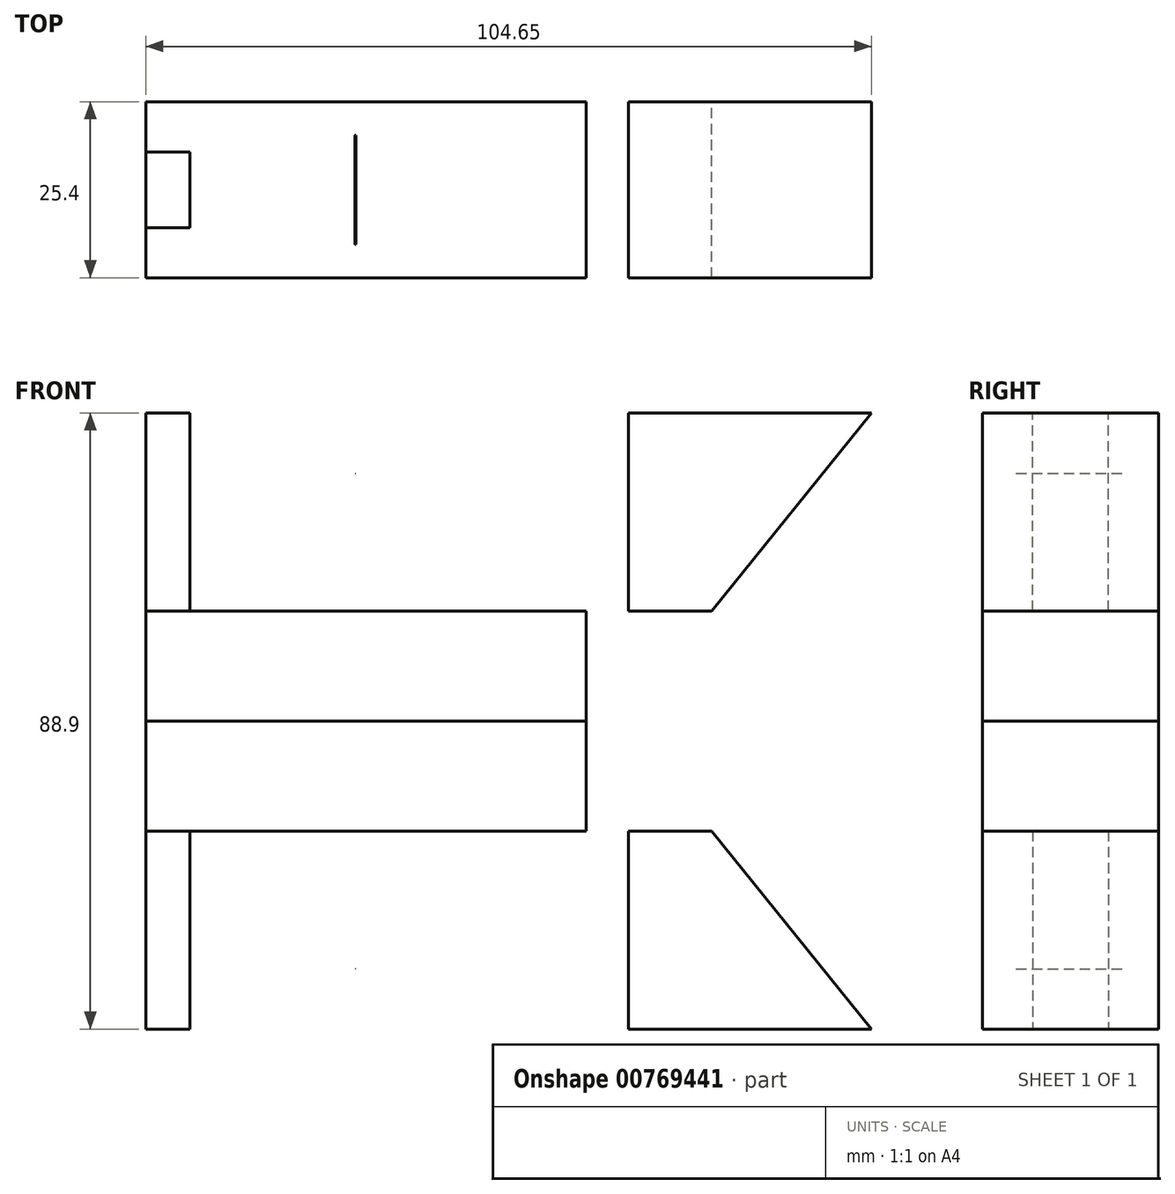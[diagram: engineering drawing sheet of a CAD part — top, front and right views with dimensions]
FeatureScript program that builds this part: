
annotation { "Feature Type Name" : "Feature", "Feature Type Description" : "" }
export const myFeature = defineFeature(function(context is Context, id is Id, definition is map)
    precondition{}
    {
        {
            var Q0;
            Q0=qCreatedBy(makeId("Front.planeOp"),FACE);
            var sketch = newSketch(context, id + "F0", { "sketchPlane" : qUnion([Q0])});
            skLineSegment(sketch, "E0.bottom", {"start": v(-31.75, 7.94) * mm, "end": v(31.75, 7.94) * mm});
            skLineSegment(sketch, "E0.top", {"start": v(-31.75, -7.94) * mm, "end": v(31.75, -7.94) * mm});
            skLineSegment(sketch, "E0.left", {"start": v(-31.75, 7.94) * mm, "end": v(-31.75, -7.94) * mm});
            skLineSegment(sketch, "E0.right", {"start": v(31.75, 7.94) * mm, "end": v(31.75, -7.94) * mm});
            skPoint(sketch, "E0.middle", {"position": v(0, 0) * mm});
            skLineSegment(sketch, "E1.bottom", {"start": v(-31.75, 7.94) * mm, "end": v(72.9, 7.94) * mm});
            skLineSegment(sketch, "E1.top", {"start": v(-31.75, 36.51) * mm, "end": v(72.9, 36.51) * mm});
            skLineSegment(sketch, "E1.left", {"start": v(-31.75, 7.94) * mm, "end": v(-31.75, 36.51) * mm});
            skLineSegment(sketch, "E1.right", {"start": v(72.9, 7.94) * mm, "end": v(72.9, 36.51) * mm});
            skLineSegment(sketch, "E2", {"start": v(-25.4, 36.51) * mm, "end": v(-25.4, 7.94) * mm});
            skLineSegment(sketch, "E3", {"start": v(72.9, 36.51) * mm, "end": v(49.83, 7.94) * mm});
            skLineSegment(sketch, "E4", {"start": v(-31.75, 22.23) * mm, "end": v(-7.11, 22.23) * mm});
            skLineSegment(sketch, "E5", {"start": v(-7.11, 22.23) * mm, "end": v(27.94, 22.23) * mm});
            skCircle(sketch, "E6", {"center": v(-1.52, 22.23) * mm, "radius": 5.59 * mm});
            skCircle(sketch, "E7", {"center": v(22.05, 22.23) * mm, "radius": 5.59 * mm});
            skLineSegment(sketch, "E8", {"start": v(-1.56, 27.81) * mm, "end": v(22.05, 27.81) * mm});
            skLineSegment(sketch, "E9", {"start": v(-1.44, 16.64) * mm, "end": v(22.05, 16.64) * mm});
            skLineSegment(sketch, "E10", {"start": v(37.85, 36.51) * mm, "end": v(37.85, 7.94) * mm});
            skLineSegment(sketch, "E11", {"start": v(37.85, 18.99) * mm, "end": v(58.75, 18.99) * mm});
            skSolve(sketch);
        }
        {
            var Q0;
            Q0=makeQuery(id+"F0.imprint","IMPRINT",FACE,{"disambiguationData":[TD([[makeQuery(id+"F0.imprint","IMPRINT",EDGE,{"derivedFrom":sQuery(id+"F0.wireOp",EDGE,"E0.top")}),1.0]])]});
            var Q1;
            {var subQ5=sQuery(id+"F0.wireOp",EDGE,"E11");Q1=makeQuery(id+"F0.imprint","IMPRINT",FACE,{"disambiguationData":[TD([[makeQuery(id+"F0.imprint","IMPRINT",EDGE,{"derivedFrom":subQ5}),1.0]])]});}
            var Q2;
            {var subQ5=sQuery(id+"F0.wireOp",EDGE,"E11");Q2=makeQuery(id+"F0.imprint","IMPRINT",FACE,{"disambiguationData":[TD([[makeQuery(id+"F0.imprint","IMPRINT",EDGE,{"derivedFrom":subQ5}),-1.0]])]});}
            extrude(context, id + "F1", {"entities" : qUnion([Q0, Q1, Q2]), "depth" : 25.4 * mm, "offsetDistance" : 25.4 * mm, "symmetric" : true});
        }
        {
            var Q0;
            {var subQ7=sQuery(id+"F0.wireOp",EDGE,"E8");Q0=makeQuery(id+"F0.imprint","IMPRINT",FACE,{"disambiguationData":[TD([[makeQuery(id+"F0.imprint","IMPRINT",EDGE,{"derivedFrom":subQ7}),1.0]])]});}
            extrude(context, id + "F2", {"entities" : qUnion([Q0]), "depth" : 15.75 * mm, "offsetDistance" : 25.4 * mm, "symmetric" : true});
        }
        {
            var Q0;
            {var subQ0=sQuery(id+"F0.wireOp",EDGE,"E1.left");var subQ1=sQuery(id+"F0.wireOp",EDGE,"E1.top");var subQ2=makeQuery(id+"F0.imprint","INTERSECT",VERTEX,{"derivedFrom":[subQ1,subQ0]});Q0=makeQuery(id+"F0.imprint","IMPRINT",FACE,{"disambiguationData":[TD([[makeQuery(id+"F0.imprint","IMPRINT",EDGE,{"disambiguationData":[TD([[subQ2,-1.0]])],"derivedFrom":subQ1}),-1.0]])]});}
            var Q1;
            {var subQ1=sQuery(id+"F0.wireOp",EDGE,"E1.bottom");var subQ3=sQuery(id+"F0.wireOp",EDGE,"E2");var subQ4=makeQuery(id+"F0.imprint","INTERSECT",VERTEX,{"derivedFrom":[subQ1,subQ3]});Q1=makeQuery(id+"F0.imprint","IMPRINT",FACE,{"disambiguationData":[TD([[makeQuery(id+"F0.imprint","IMPRINT",EDGE,{"disambiguationData":[TD([[subQ4,1.0]])],"derivedFrom":subQ3}),-1.0]])]});}
            extrude(context, id + "F3", {"entities" : qUnion([Q0, Q1]), "depth" : 10.92 * mm, "offsetDistance" : 25.4 * mm, "symmetric" : true});
        }
        {
            var Q0;
            Q0=makeQuery(id+"F3.opExtrude","SWEPT_BODY",BODY,{"disambiguationData":[OSD([sQuery(id+"F0.wireOp",EDGE,"E1.bottom"),sQuery(id+"F0.wireOp",EDGE,"E1.top"),sQuery(id+"F0.wireOp",EDGE,"E1.left"),sQuery(id+"F0.wireOp",EDGE,"E2")])]});
            var Q1;
            Q1=makeQuery(id+"F2.opExtrude","SWEPT_BODY",BODY,{"disambiguationData":[OSD([sQuery(id+"F0.wireOp",EDGE,"E1.bottom"),sQuery(id+"F0.wireOp",EDGE,"E1.top"),sQuery(id+"F0.wireOp",EDGE,"E2"),sQuery(id+"F0.wireOp",EDGE,"E6"),sQuery(id+"F0.wireOp",EDGE,"E7"),sQuery(id+"F0.wireOp",EDGE,"E8"),sQuery(id+"F0.wireOp",EDGE,"E9"),sQuery(id+"F0.wireOp",EDGE,"E10")])]});
            var Q2;
            Q2=makeQuery(id+"F1.opExtrude","SWEPT_BODY",BODY,{"disambiguationData":[OSD([sQuery(id+"F0.wireOp",EDGE,"E1.bottom"),sQuery(id+"F0.wireOp",EDGE,"E1.top"),sQuery(id+"F0.wireOp",EDGE,"E3"),sQuery(id+"F0.wireOp",EDGE,"E10")])]});
            var Q3;
            Q3=makeQuery(id+"F1.opExtrude","SWEPT_BODY",BODY,{"disambiguationData":[OSD([sQuery(id+"F0.wireOp",EDGE,"E0.top"),sQuery(id+"F0.wireOp",EDGE,"E0.left"),sQuery(id+"F0.wireOp",EDGE,"E0.right"),sQuery(id+"F0.wireOp",EDGE,"E1.bottom")])]});
            var Q4;
            Q4=makeQuery(id+"F1.opExtrude","SWEPT_FACE",FACE,{"disambiguationData":[OSD([sQuery(id+"F0.wireOp",EDGE,"E0.top")])]});
            mirror(context, id + "F4", {"entities" : qUnion([Q0, Q1, Q2, Q3]), "mirrorPlane" : qUnion([Q4])});
        }
    });
